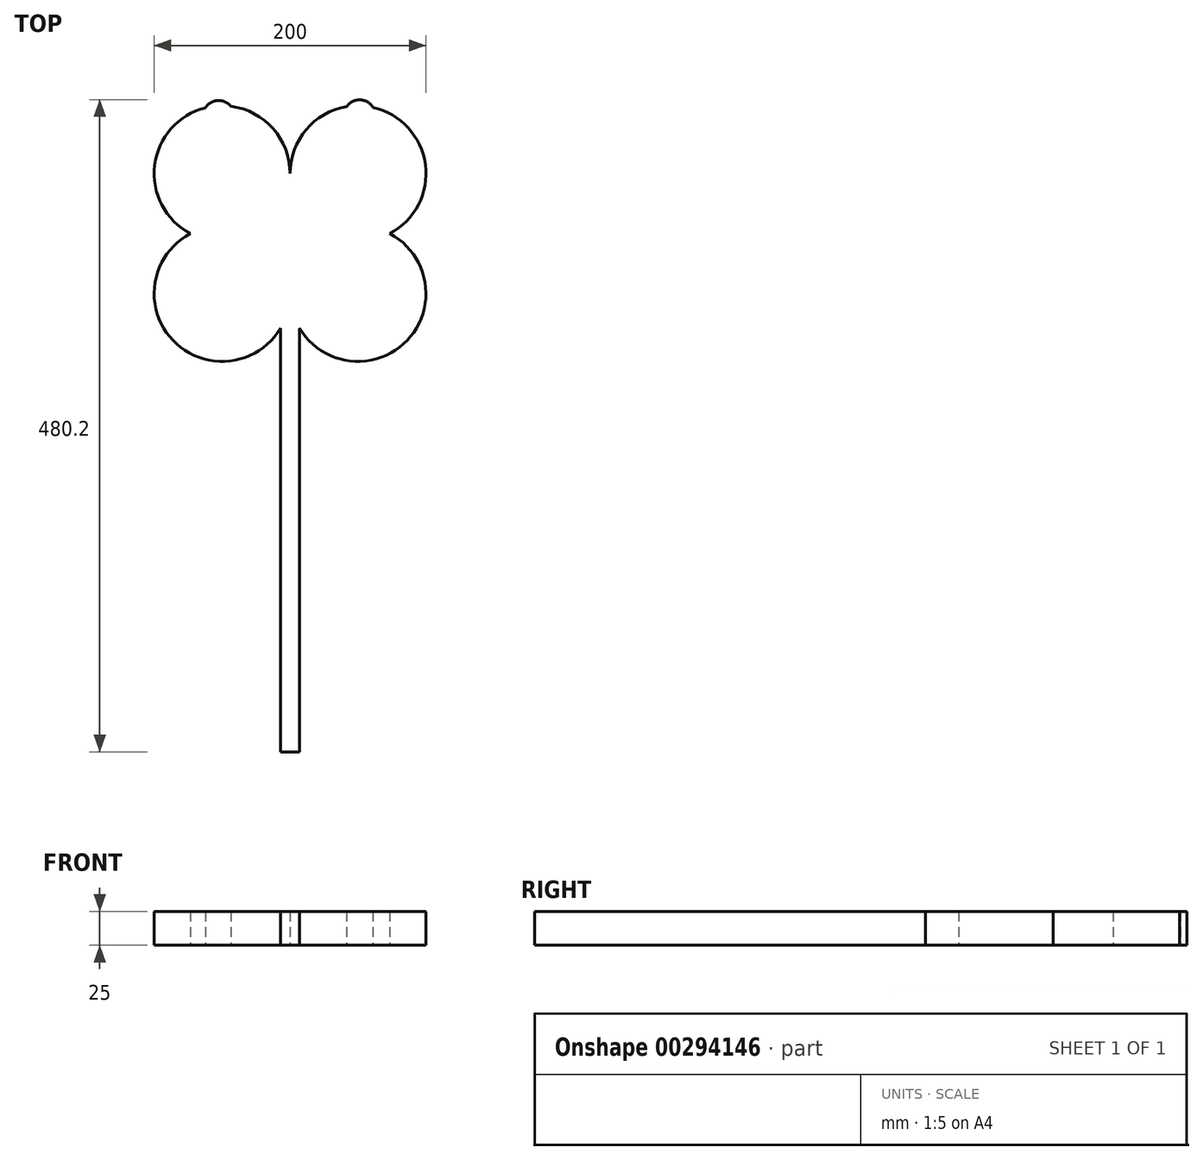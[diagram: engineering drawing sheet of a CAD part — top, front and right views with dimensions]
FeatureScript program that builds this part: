
annotation { "Feature Type Name" : "Feature", "Feature Type Description" : "" }
export const myFeature = defineFeature(function(context is Context, id is Id, definition is map)
    precondition{}
    {
        {
            var Q0;
            Q0=qCreatedBy(makeId("Top.planeOp"),FACE);
            var sketch = newSketch(context, id + "F0", { "sketchPlane" : qUnion([Q0])});
            skPoint(sketch, "E0.visualSharp", {"position": v(-170.23, -1.01) * mm});
            skPoint(sketch, "E1.visualSharp", {"position": v(-154.03, -3.73) * mm});
            skPoint(sketch, "E2.center.orphan", {"position": v(-127.81, -4.64) * mm});
            skPoint(sketch, "E3.end.orphan", {"position": v(-143.12, 0) * mm});
            skPoint(sketch, "E4.right.end.orphan", {"position": v(-127.81, 3.4) * mm});
            skPoint(sketch, "E4.bottom.end.orphan", {"position": v(-127.81, -12.68) * mm});
            skArc(sketch, "E5", {"start": v(-15.96, 45.2) * mm, "mid": v(-28.4, 78.2) * mm, "end": v(-59.52, 94.79) * mm});
            skArc(sketch, "E6", {"start": v(-15.96, -43.16) * mm, "mid": v(59.82, -86) * mm, "end": v(57.46, 1.02) * mm});
            skArc(sketch, "E7", {"start": v(-89.37, 1.02) * mm, "mid": v(-91.74, -86) * mm, "end": v(-15.96, -43.16) * mm});
            skArc(sketch, "E8.trimOffspring", {"start": v(57.46, 1.02) * mm, "mid": v(83.6, 51.78) * mm, "end": v(45.12, 93.96) * mm});
            skPoint(sketch, "E9.centerSnap0", {"position": v(59.82, 88.04) * mm});
            skPoint(sketch, "E9.center.orphan", {"position": v(35.25, 88.04) * mm});
            skLineSegment(sketch, "E10.left", {"start": v(-8.96, -68.67) * mm, "end": v(-8.96, -234.5) * mm});
            skLineSegment(sketch, "E10.right", {"start": v(-22.96, -68.67) * mm, "end": v(-22.96, -234.5) * mm});
            skPoint(sketch, "E11.orphan", {"position": v(-8.96, -43.16) * mm});
            skPoint(sketch, "E10.bottom.end.orphan", {"position": v(-22.96, -43.16) * mm});
            skArc(sketch, "E12", {"start": v(-59.52, 94.79) * mm, "mid": v(-69.14, 99.04) * mm, "end": v(-78.2, 93.68) * mm});
            skArc(sketch, "E13", {"start": v(45.12, 93.96) * mm, "mid": v(35.58, 99.54) * mm, "end": v(25.74, 94.5) * mm});
            skArc(sketch, "E14.trimOffspring", {"start": v(25.74, 94.5) * mm, "mid": v(-4.13, 77.5) * mm, "end": v(-15.96, 45.2) * mm});
            skArc(sketch, "E15.trimOffspring", {"start": v(-78.2, 93.68) * mm, "mid": v(-115.6, 51.2) * mm, "end": v(-89.37, 1.02) * mm});
            skLineSegment(sketch, "E16.top", {"start": v(-8.96, -380.66) * mm, "end": v(-22.96, -380.66) * mm});
            skLineSegment(sketch, "E16.left", {"start": v(-8.96, -234.5) * mm, "end": v(-8.96, -380.66) * mm});
            skLineSegment(sketch, "E16.right", {"start": v(-22.96, -234.5) * mm, "end": v(-22.96, -380.66) * mm});
            skPoint(sketch, "E17.centerSnap0", {"position": v(-15.96, -380.66) * mm});
            skPoint(sketch, "E18.center.orphan", {"position": v(45.56, -56.25) * mm});
            skPoint(sketch, "E19.center.orphan", {"position": v(-76.9, -56.25) * mm});
            skPoint(sketch, "E17.center.orphan", {"position": v(-15.96, -356.8) * mm});
            skLineSegment(sketch, "E20.bottom", {"start": v(-8.96, -43.16) * mm, "end": v(-22.96, -43.16) * mm});
            skLineSegment(sketch, "E20.left", {"start": v(-8.96, -43.16) * mm, "end": v(-8.96, -380.66) * mm});
            skLineSegment(sketch, "E20.right", {"start": v(-22.96, -43.16) * mm, "end": v(-22.96, -380.66) * mm});
            skSolve(sketch);
        }
        {
            var Q0;
            Q0 = qSketchRegion(id + "F0", true);
            extrude(context, id + "F1", {"entities" : qUnion([Q0]), "depth" : 25 * mm});
        }
        {
            var Q0;
            Q0 = qSketchRegion(id + "F0", true);
            extrude(context, id + "F2", {"entities" : qUnion([Q0]), "operationType" : NewBodyOperationType.ADD, "depth" : 25 * mm});
        }
    });
